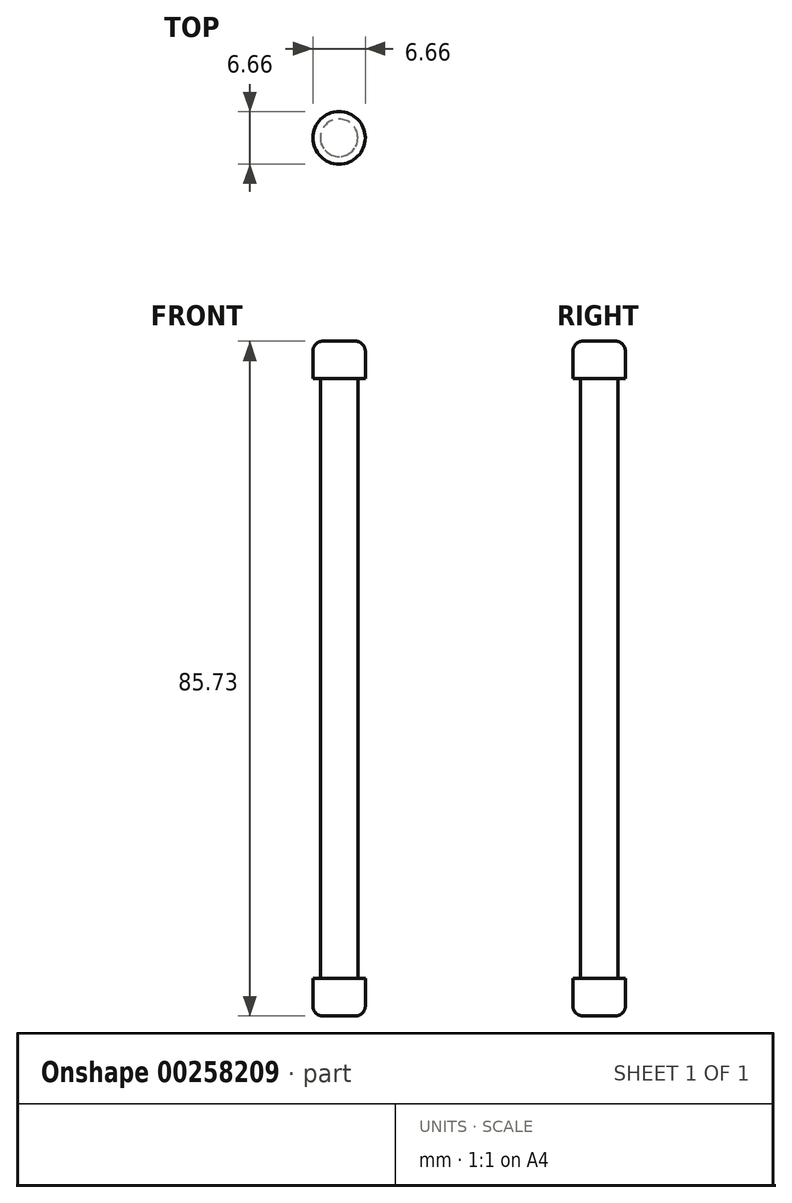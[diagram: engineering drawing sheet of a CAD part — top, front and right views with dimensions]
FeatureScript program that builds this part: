
annotation { "Feature Type Name" : "Feature", "Feature Type Description" : "" }
export const myFeature = defineFeature(function(context is Context, id is Id, definition is map)
    precondition{}
    {
        {
            var Q0;
            Q0=qCreatedBy(makeId("Top.planeOp"),FACE);
            var sketch = newSketch(context, id + "F0", { "sketchPlane" : qUnion([Q0])});
            skCircle(sketch, "E0", {"center": v(0, 0) * mm, "radius": 2.38 * mm});
            skSolve(sketch);
        }
        {
            var Q0;
            Q0 = qSketchRegion(id + "F0", true);
            extrude(context, id + "F1", {"entities" : qUnion([Q0]), "depth" : 85.72 * mm});
        }
        {
            var Q0;
            Q0=makeQuery(id+"F1.opExtrude","CAP_FACE",FACE,{"disambiguationData":[OSD([sQuery(id+"F0.wireOp",EDGE,"E0")])],"isStart":false});
            var sketch = newSketch(context, id + "F2", { "sketchPlane" : qUnion([Q0])});
            skCircle(sketch, "E1", {"center": v(0, 0) * mm, "radius": 3.33 * mm});
            skSolve(sketch);
        }
        {
            var Q0;
            Q0 = qSketchRegion(id + "F2", true);
            extrude(context, id + "F3", {"entities" : qUnion([Q0]), "operationType" : NewBodyOperationType.ADD, "oppositeDirection" : true, "depth" : 4.76 * mm});
        }
        {
            var Q0;
            Q0=makeQuery(id+"F3.opExtrude","CAP_EDGE",EDGE,{"disambiguationData":[OSD([sQuery(id+"F2.wireOp",EDGE,"E1")])],"isStart":true});
            fillet(context, id + "F4", {"entities" : qUnion([Q0]), "radius" : 1.27 * mm, "tangentPropagation" : true, "allowEdgeOverflow" : false});
        }
        {
            var Q0;
            Q0=makeQuery(id+"F1.opExtrude","CAP_FACE",FACE,{"disambiguationData":[OSD([sQuery(id+"F0.wireOp",EDGE,"E0")])],"isStart":true});
            var sketch = newSketch(context, id + "F5", { "sketchPlane" : qUnion([Q0])});
            skCircle(sketch, "E2", {"center": v(0, 0) * mm, "radius": 3.33 * mm});
            skSolve(sketch);
        }
        {
            var Q0;
            Q0 = qSketchRegion(id + "F5", true);
            extrude(context, id + "F6", {"entities" : qUnion([Q0]), "operationType" : NewBodyOperationType.ADD, "oppositeDirection" : true, "depth" : 4.76 * mm});
        }
        {
            var Q0;
            Q0=makeQuery(id+"F6.opExtrude","CAP_EDGE",EDGE,{"disambiguationData":[OSD([sQuery(id+"F5.wireOp",EDGE,"E2")])],"isStart":true});
            fillet(context, id + "F7", {"entities" : qUnion([Q0]), "radius" : 1.27 * mm, "tangentPropagation" : true, "allowEdgeOverflow" : false});
        }
    });
